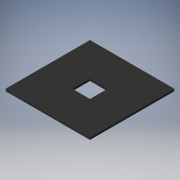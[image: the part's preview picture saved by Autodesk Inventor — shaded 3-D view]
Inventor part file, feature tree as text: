
AUTODESK INVENTOR PART (.ipt)
format: ipt  version: 2019 (Build 230136000, 136)  size: 98,304 bytes
history: native  units: in
note: dims shown in document units (in); Inventor stores cm internally (conversion verified against a paired STEP export)
features: extrude x1, sketch x1
ambient origin geometry x8: Origin, YZ Plane, XZ Plane, XY Plane, X Axis, Y Axis, Z Axis, Center Point
bodies: Solid1 (feature_tree)
feature tree (2):
  extrude  "Extrusion1"  Depth=14.0in
  sketch  "Sketch1"  dims[d0=14.0in d1=14.0in d2=0.375in d3=0.0in d4=3.0in]
